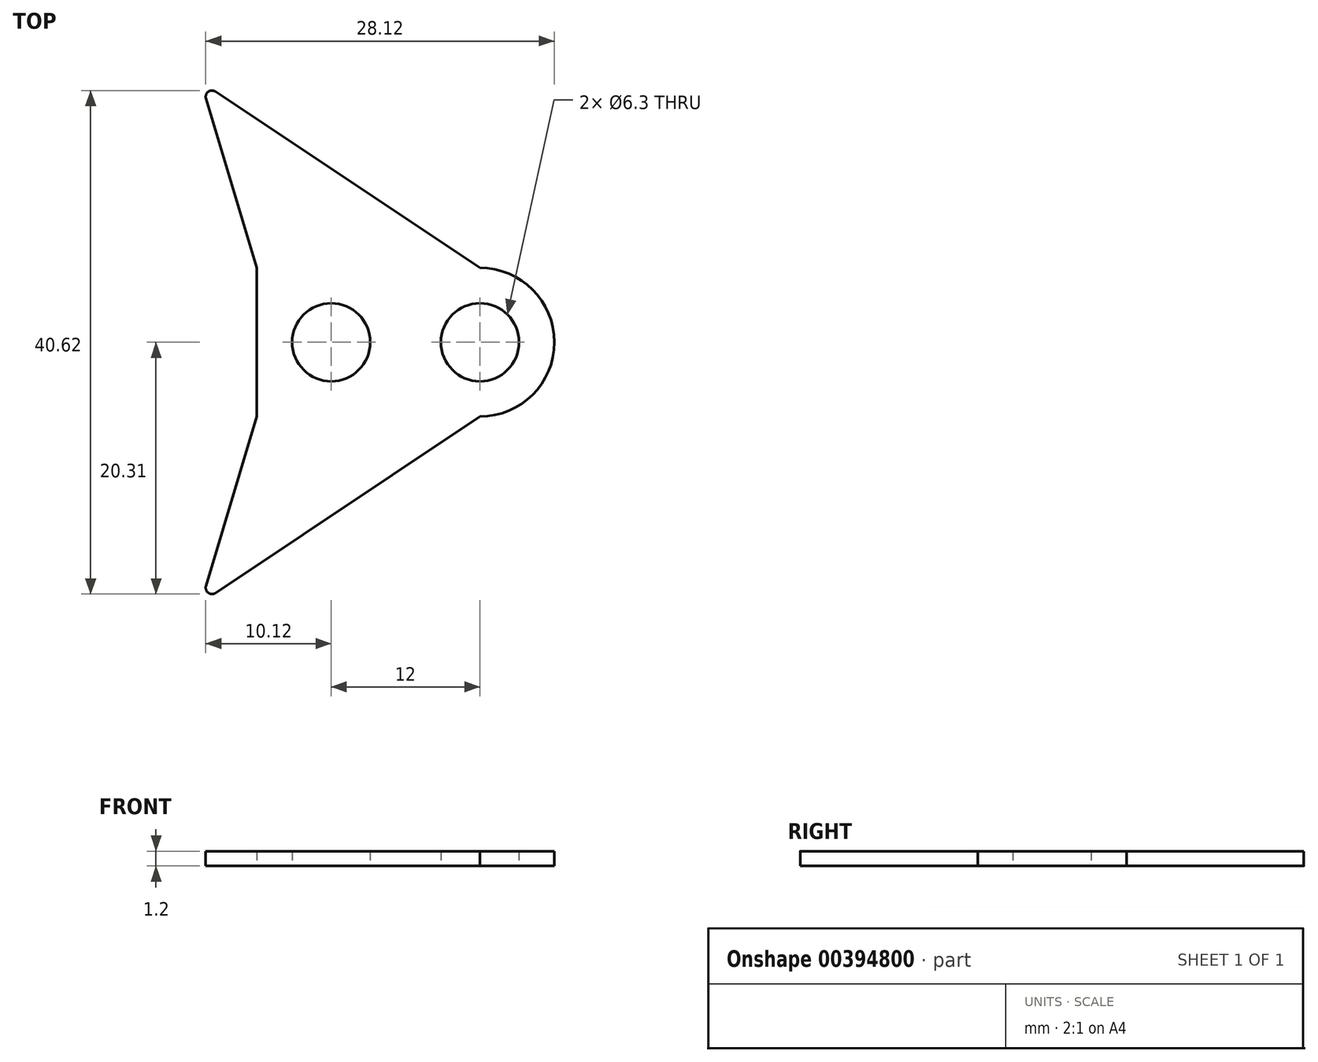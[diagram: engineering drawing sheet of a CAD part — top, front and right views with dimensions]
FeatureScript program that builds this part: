
annotation { "Feature Type Name" : "Feature", "Feature Type Description" : "" }
export const myFeature = defineFeature(function(context is Context, id is Id, definition is map)
    precondition{}
    {
        {
            var Q0;
            Q0=qCreatedBy(makeId("Top.planeOp"),FACE);
            var sketch = newSketch(context, id + "F0", { "sketchPlane" : qUnion([Q0])});
            skLineSegment(sketch, "E0.bottom", {"start": v(0, 0) * mm, "end": v(18, 0) * mm});
            skLineSegment(sketch, "E0.top", {"start": v(0, -12) * mm, "end": v(18, -12) * mm});
            skLineSegment(sketch, "E0.left", {"start": v(0, 0) * mm, "end": v(0, -12) * mm});
            skLineSegment(sketch, "E0.right", {"start": v(18, 0) * mm, "end": v(18, -12) * mm, "construction": true});
            skArc(sketch, "E1", {"start": v(18, -12) * mm, "mid": v(24, -6) * mm, "end": v(18, 0) * mm});
            skLineSegment(sketch, "E2", {"start": v(0, 0) * mm, "end": v(-4.5, 15) * mm});
            skLineSegment(sketch, "E3", {"start": v(-4.5, 15) * mm, "end": v(18, 0) * mm});
            skLineSegment(sketch, "E4", {"start": v(0, -12) * mm, "end": v(-4.5, -27) * mm});
            skLineSegment(sketch, "E5", {"start": v(-4.5, -27) * mm, "end": v(18, -12) * mm});
            skCircle(sketch, "E6", {"center": v(18, -6) * mm, "radius": 3.15 * mm});
            skLineSegment(sketch, "E7", {"start": v(6, 0) * mm, "end": v(6, -12) * mm, "construction": true});
            skCircle(sketch, "E8", {"center": v(6, -6) * mm, "radius": 3.15 * mm});
            skSolve(sketch);
        }
        {
            var Q0;
            Q0 = qSketchRegion(id + "F0", true);
            extrude(context, id + "F1", {"entities" : qUnion([Q0]), "depth" : 1.2 * mm});
        }
        {
            var Q0;
            Q0=makeQuery(id+"F1.opExtrude","SWEPT_EDGE",EDGE,{"disambiguationData":[OSD([sQuery(id+"F0.wireOp",EDGE,"E4"),sQuery(id+"F0.wireOp",EDGE,"E5")])]});
            var Q1;
            Q1=makeQuery(id+"F1.opExtrude","SWEPT_EDGE",EDGE,{"disambiguationData":[OSD([sQuery(id+"F0.wireOp",EDGE,"E2"),sQuery(id+"F0.wireOp",EDGE,"E3")])]});
            fillet(context, id + "F2", {"entities" : qUnion([Q0, Q1]), "radius" : 0.5 * mm, "tangentPropagation" : true, "allowEdgeOverflow" : false});
        }
    });
